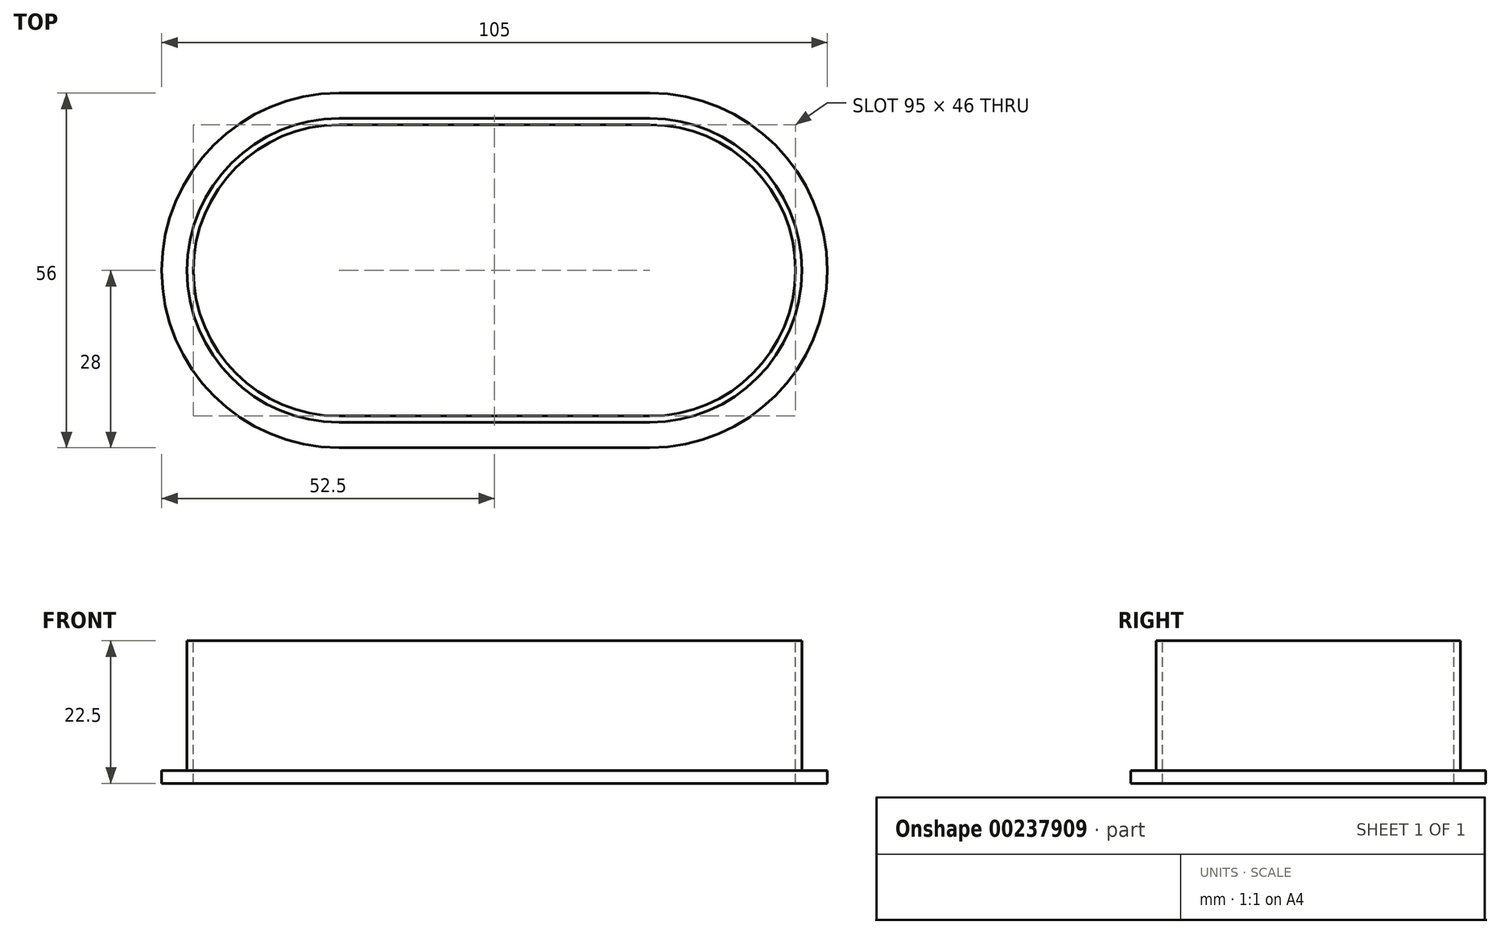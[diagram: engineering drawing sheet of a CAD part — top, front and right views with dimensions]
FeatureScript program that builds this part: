
annotation { "Feature Type Name" : "Feature", "Feature Type Description" : "" }
export const myFeature = defineFeature(function(context is Context, id is Id, definition is map)
    precondition{}
    {
        {
            var Q0;
            Q0=qCreatedBy(makeId("Top.planeOp"),FACE);
            var sketch = newSketch(context, id + "F0", { "sketchPlane" : qUnion([Q0])});
            skArc(sketch, "E0", {"start": v(0, 24) * mm, "mid": v(-24, 0) * mm, "end": v(0, -24) * mm});
            skArc(sketch, "E1", {"start": v(0, 23) * mm, "mid": v(-23, 0) * mm, "end": v(0, -23) * mm});
            skArc(sketch, "E2", {"start": v(0, 28) * mm, "mid": v(-28, 0) * mm, "end": v(0, -28) * mm});
            skArc(sketch, "E3", {"start": v(49, -28) * mm, "mid": v(77, 0) * mm, "end": v(49, 28) * mm});
            skArc(sketch, "E4", {"start": v(49, -23) * mm, "mid": v(72, 0) * mm, "end": v(49, 23) * mm});
            skLineSegment(sketch, "E5", {"start": v(49, 28) * mm, "end": v(0, 28) * mm});
            skLineSegment(sketch, "E6", {"start": v(0, -28) * mm, "end": v(49, -28) * mm});
            skLineSegment(sketch, "E7", {"start": v(0, -23) * mm, "end": v(49, -23) * mm});
            skLineSegment(sketch, "E8", {"start": v(49, 23) * mm, "end": v(0, 23) * mm});
            skArc(sketch, "E9", {"start": v(49, -24) * mm, "mid": v(73, 0) * mm, "end": v(49, 24) * mm});
            skLineSegment(sketch, "E10", {"start": v(49, 24) * mm, "end": v(0, 24) * mm});
            skLineSegment(sketch, "E11", {"start": v(0, -24) * mm, "end": v(49, -24) * mm});
            skSolve(sketch);
        }
        {
            var Q0;
            Q0=makeQuery(id+"F0.imprint","IMPRINT",FACE,{"disambiguationData":[TD([[makeQuery(id+"F0.imprint","IMPRINT",EDGE,{"derivedFrom":sQuery(id+"F0.wireOp",EDGE,"E0")}),-1.0]])]});
            var Q1;
            Q1=makeQuery(id+"F0.imprint","IMPRINT",FACE,{"disambiguationData":[TD([[makeQuery(id+"F0.imprint","IMPRINT",EDGE,{"derivedFrom":sQuery(id+"F0.wireOp",EDGE,"E0")}),1.0]])]});
            extrude(context, id + "F1", {"entities" : qUnion([Q0, Q1]), "oppositeDirection" : true, "depth" : 2 * mm, "offsetDistance" : 25 * mm});
        }
        {
            var Q0;
            Q0=makeQuery(id+"F0.imprint","IMPRINT",FACE,{"disambiguationData":[TD([[makeQuery(id+"F0.imprint","IMPRINT",EDGE,{"derivedFrom":sQuery(id+"F0.wireOp",EDGE,"E0")}),1.0]])]});
            extrude(context, id + "F2", {"entities" : qUnion([Q0]), "operationType" : NewBodyOperationType.ADD, "depth" : 20.5 * mm, "offsetDistance" : 25 * mm});
        }
    });
